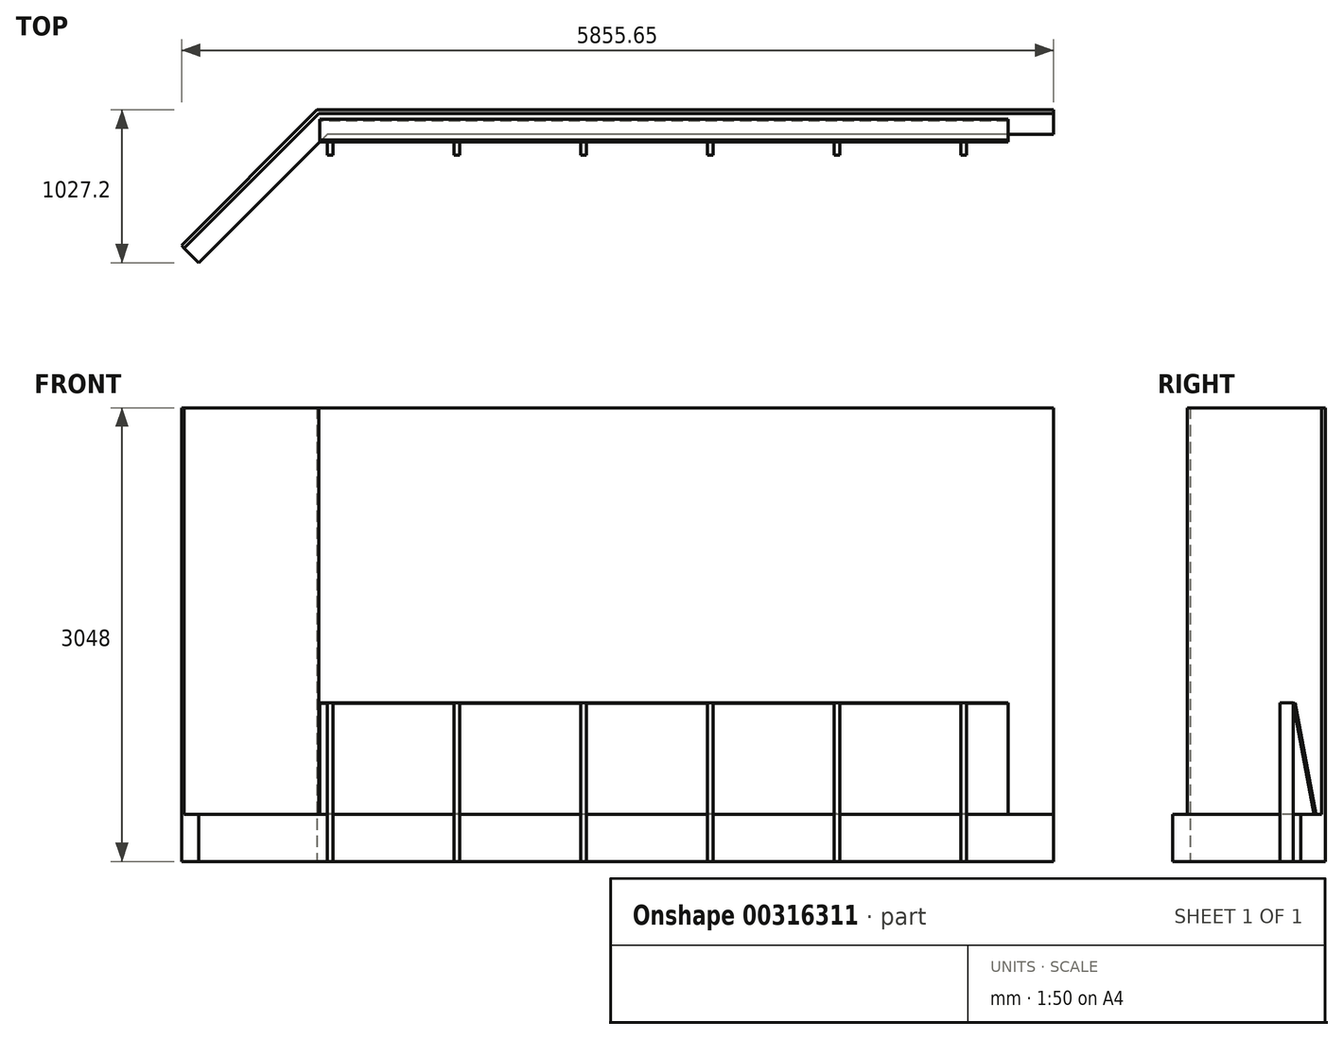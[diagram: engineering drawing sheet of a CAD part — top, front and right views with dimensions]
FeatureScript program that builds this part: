
annotation { "Feature Type Name" : "Feature", "Feature Type Description" : "" }
export const myFeature = defineFeature(function(context is Context, id is Id, definition is map)
    precondition{}
    {
        {
            var Q0;
            Q0=qCreatedBy(makeId("Top.planeOp"),FACE);
            var sketch = newSketch(context, id + "F0", { "sketchPlane" : qUnion([Q0])});
            skLineSegment(sketch, "E0", {"start": v(0, 0) * mm, "end": v(4934.67, 0) * mm});
            skLineSegment(sketch, "E1", {"start": v(4934.67, 0) * mm, "end": v(4934.67, -139.7) * mm});
            skLineSegment(sketch, "E2", {"start": v(4934.67, -139.7) * mm, "end": v(57.87, -139.7) * mm});
            skLineSegment(sketch, "E3", {"start": v(57.87, -139.7) * mm, "end": v(-804.24, -1001.8) * mm});
            skLineSegment(sketch, "E4", {"start": v(-804.24, -1001.8) * mm, "end": v(-903.02, -903.02) * mm});
            skLineSegment(sketch, "E5", {"start": v(-903.02, -903.02) * mm, "end": v(0, 0) * mm});
            skSolve(sketch);
        }
        {
            var Q0;
            Q0=makeQuery(id+"F0.imprint","IMPRINT",FACE,{"disambiguationData":[TD([[makeQuery(id+"F0.imprint","IMPRINT",EDGE,{"derivedFrom":sQuery(id+"F0.wireOp",EDGE,"E0")}),-1.0]])]});
            extrude(context, id + "F1", {"entities" : qUnion([Q0]), "depth" : 317.5 * mm});
        }
        {
            var Q0;
            Q0=makeQuery(id+"F1.opExtrude","CAP_FACE",FACE,{"disambiguationData":[OSD([sQuery(id+"F0.wireOp",EDGE,"E0"),sQuery(id+"F0.wireOp",EDGE,"E1"),sQuery(id+"F0.wireOp",EDGE,"E2"),sQuery(id+"F0.wireOp",EDGE,"E3"),sQuery(id+"F0.wireOp",EDGE,"E4"),sQuery(id+"F0.wireOp",EDGE,"E5")])],"isStart":true});
            var sketch = newSketch(context, id + "F2", { "sketchPlane" : qUnion([Q0])});
            skLineSegment(sketch, "E6", {"start": v(-903.02, 903.02) * mm, "end": v(-920.98, 885.06) * mm});
            skLineSegment(sketch, "E7", {"start": v(-920.98, 885.06) * mm, "end": v(-10.52, -25.4) * mm});
            skLineSegment(sketch, "E8", {"start": v(-10.52, -25.4) * mm, "end": v(4934.67, -25.4) * mm});
            skLineSegment(sketch, "E9", {"start": v(4934.67, -25.4) * mm, "end": v(4934.67, 0) * mm});
            skLineSegment(sketch, "E10.1", {"start": v(0, 0) * mm, "end": v(4934.67, 0) * mm});
            skLineSegment(sketch, "E10.2", {"start": v(-903.02, 903.02) * mm, "end": v(0, 0) * mm});
            skSolve(sketch);
        }
        {
            var Q0;
            Q0 = qSketchRegion(id + "F2", true);
            extrude(context, id + "F3", {"entities" : qUnion([Q0]), "operationType" : NewBodyOperationType.ADD, "oppositeDirection" : true, "depth" : 3048 * mm});
        }
        {
            var Q0;
            Q0=makeQuery(id+"F3.boolean.opBoolean","MERGE",FACE,{"derivedFrom":[makeQuery(id+"F1.opExtrude","CAP_FACE",FACE,{"disambiguationData":[OSD([sQuery(id+"F0.wireOp",EDGE,"E0"),sQuery(id+"F0.wireOp",EDGE,"E1"),sQuery(id+"F0.wireOp",EDGE,"E2"),sQuery(id+"F0.wireOp",EDGE,"E3"),sQuery(id+"F0.wireOp",EDGE,"E4"),sQuery(id+"F0.wireOp",EDGE,"E5")])],"isStart":true}),makeQuery(id+"F3.opExtrude","CAP_FACE",FACE,{"disambiguationData":[OSD([sQuery(id+"F2.wireOp",EDGE,"E6"),sQuery(id+"F2.wireOp",EDGE,"E7"),sQuery(id+"F2.wireOp",EDGE,"E8"),sQuery(id+"F2.wireOp",EDGE,"E9"),sQuery(id+"F2.wireOp",EDGE,"E10.1"),sQuery(id+"F2.wireOp",EDGE,"E10.2")])],"isStart":true})]});
            var sketch = newSketch(context, id + "F4", { "sketchPlane" : qUnion([Q0])});
            skLineSegment(sketch, "E11.bottom", {"start": v(57.87, 190.5) * mm, "end": v(95.97, 190.5) * mm});
            skLineSegment(sketch, "E11.top", {"start": v(57.87, 279.4) * mm, "end": v(95.97, 279.4) * mm});
            skLineSegment(sketch, "E11.left", {"start": v(57.87, 190.5) * mm, "end": v(57.87, 279.4) * mm});
            skLineSegment(sketch, "E11.right", {"start": v(95.97, 190.5) * mm, "end": v(95.97, 279.4) * mm});
            skLineSegment(sketch, "E12.bottom", {"start": v(908.77, 279.4) * mm, "end": v(946.87, 279.4) * mm});
            skLineSegment(sketch, "E12.top", {"start": v(908.77, 190.5) * mm, "end": v(946.87, 190.5) * mm});
            skLineSegment(sketch, "E12.left", {"start": v(908.77, 279.4) * mm, "end": v(908.77, 190.5) * mm});
            skLineSegment(sketch, "E12.right", {"start": v(946.87, 279.4) * mm, "end": v(946.87, 190.5) * mm});
            skLineSegment(sketch, "E13.bottom", {"start": v(1759.67, 279.4) * mm, "end": v(1797.77, 279.4) * mm});
            skLineSegment(sketch, "E13.top", {"start": v(1759.67, 190.5) * mm, "end": v(1797.77, 190.5) * mm});
            skLineSegment(sketch, "E13.left", {"start": v(1759.67, 279.4) * mm, "end": v(1759.67, 190.5) * mm});
            skLineSegment(sketch, "E13.right", {"start": v(1797.77, 279.4) * mm, "end": v(1797.77, 190.5) * mm});
            skLineSegment(sketch, "E14.bottom", {"start": v(2610.57, 279.4) * mm, "end": v(2648.67, 279.4) * mm});
            skLineSegment(sketch, "E14.top", {"start": v(2610.57, 190.5) * mm, "end": v(2648.67, 190.5) * mm});
            skLineSegment(sketch, "E14.left", {"start": v(2610.57, 279.4) * mm, "end": v(2610.57, 190.5) * mm});
            skLineSegment(sketch, "E14.right", {"start": v(2648.67, 279.4) * mm, "end": v(2648.67, 190.5) * mm});
            skLineSegment(sketch, "E15", {"start": v(95.97, 190.5) * mm, "end": v(908.77, 190.5) * mm, "construction": true});
            skLineSegment(sketch, "E16", {"start": v(946.87, 190.5) * mm, "end": v(1759.67, 190.5) * mm, "construction": true});
            skLineSegment(sketch, "E17", {"start": v(1797.77, 190.5) * mm, "end": v(2610.57, 190.5) * mm, "construction": true});
            skLineSegment(sketch, "E18", {"start": v(57.87, 139.7) * mm, "end": v(57.87, 190.5) * mm, "construction": true});
            skLineSegment(sketch, "E19", {"start": v(2648.67, 190.5) * mm, "end": v(3461.47, 190.5) * mm, "construction": true});
            skLineSegment(sketch, "E20.bottom", {"start": v(3461.47, 190.5) * mm, "end": v(3499.57, 190.5) * mm});
            skLineSegment(sketch, "E20.top", {"start": v(3461.47, 279.4) * mm, "end": v(3499.57, 279.4) * mm});
            skLineSegment(sketch, "E20.left", {"start": v(3461.47, 190.5) * mm, "end": v(3461.47, 279.4) * mm});
            skLineSegment(sketch, "E20.right", {"start": v(3499.57, 190.5) * mm, "end": v(3499.57, 279.4) * mm});
            skLineSegment(sketch, "E21", {"start": v(3499.57, 190.5) * mm, "end": v(4312.37, 190.5) * mm, "construction": true});
            skLineSegment(sketch, "E22.bottom", {"start": v(4312.37, 190.5) * mm, "end": v(4350.47, 190.5) * mm});
            skLineSegment(sketch, "E22.top", {"start": v(4312.37, 279.4) * mm, "end": v(4350.47, 279.4) * mm});
            skLineSegment(sketch, "E22.left", {"start": v(4312.37, 190.5) * mm, "end": v(4312.37, 279.4) * mm});
            skLineSegment(sketch, "E22.right", {"start": v(4350.47, 190.5) * mm, "end": v(4350.47, 279.4) * mm});
            skSolve(sketch);
        }
        {
            var Q0;
            Q0 = qSketchRegion(id + "F4", true);
            extrude(context, id + "F5", {"entities" : qUnion([Q0]), "oppositeDirection" : true, "depth" : 1066.8 * mm});
        }
        {
            var Q0;
            Q0=makeQuery(id+"F5.opExtrude","SWEPT_FACE",FACE,{"disambiguationData":[OSD([sQuery(id+"F4.wireOp",EDGE,"E11.left")])]});
            var sketch = newSketch(context, id + "F6", { "sketchPlane" : qUnion([Q0])});
            skSolve(sketch);
        }
        {
            var Q0;
            {var subQ0=sQuery(id+"F4.wireOp",EDGE,"E11.left");Q0=makeQuery(id+"F6.imprint","IMPRINT",FACE,{"disambiguationData":[TD([[makeQuery(id+"F6.imprint","IMPRINT",EDGE,{"derivedFrom":makeQuery(id+"F5.opExtrude","CAP_EDGE",EDGE,{"disambiguationData":[OSD([subQ0])],"isStart":true})}),1.0]])]});}
            var sketch = newSketch(context, id + "F7", { "sketchPlane" : qUnion([Q0])});
            skLineSegment(sketch, "E23", {"start": v(190.5, 0) * mm, "end": v(38.1, 0) * mm, "construction": true});
            skLineSegment(sketch, "E24", {"start": v(38.1, 0) * mm, "end": v(38.1, 319.84) * mm, "construction": true});
            skLineSegment(sketch, "E25", {"start": v(38.1, 319.84) * mm, "end": v(178.02, 1066.8) * mm});
            skLineSegment(sketch, "E26", {"start": v(178.02, 1066.8) * mm, "end": v(190.5, 1064.46) * mm});
            skLineSegment(sketch, "E27", {"start": v(190.5, 1064.46) * mm, "end": v(50.58, 317.5) * mm});
            skLineSegment(sketch, "E28", {"start": v(50.58, 317.5) * mm, "end": v(38.1, 319.84) * mm});
            skLineSegment(sketch, "E29.0", {"start": v(190.5, 1066.8) * mm, "end": v(190.5, 0) * mm, "construction": true});
            skLineSegment(sketch, "E30", {"start": v(178.02, 1066.8) * mm, "end": v(190.5, 1066.8) * mm, "construction": true});
            skSolve(sketch);
        }
        {
            var Q0;
            Q0 = qSketchRegion(id + "F7", true);
            extrude(context, id + "F8", {"entities" : qUnion([Q0]), "operationType" : NewBodyOperationType.ADD, "oppositeDirection" : true, "depth" : 4572 * mm, "hasSecondDirection" : true, "secondDirectionOppositeDirection" : false, "secondDirectionDepth" : 50.8 * mm});
        }
    });
